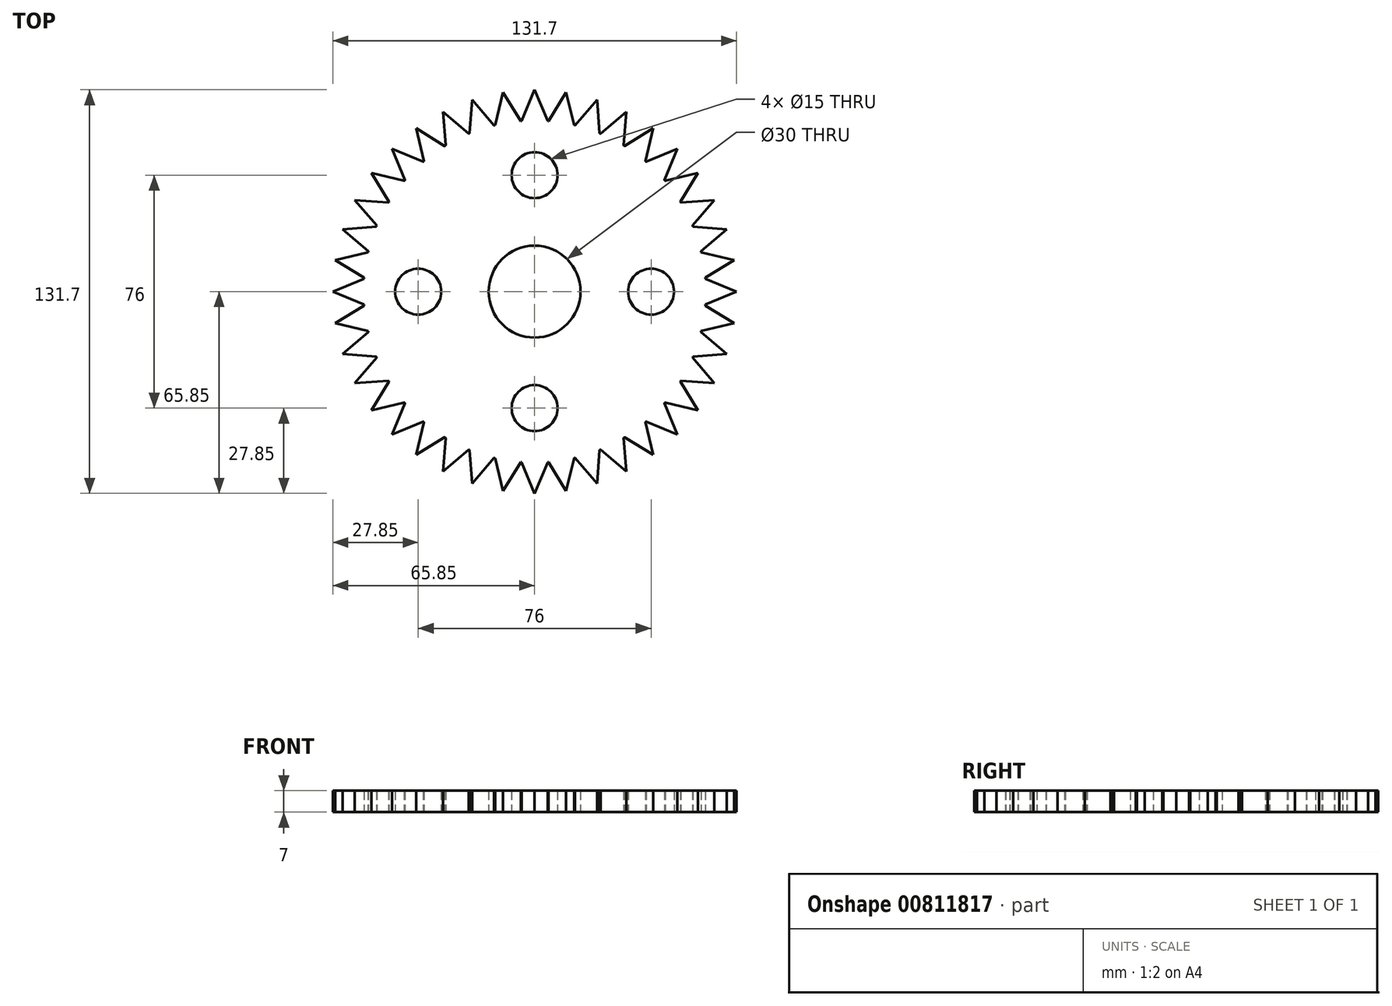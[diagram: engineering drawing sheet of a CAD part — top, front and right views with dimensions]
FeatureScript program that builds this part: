
annotation { "Feature Type Name" : "Feature", "Feature Type Description" : "" }
export const myFeature = defineFeature(function(context is Context, id is Id, definition is map)
    precondition{}
    {
        {
            var Q0;
            Q0=qCreatedBy(makeId("Top.planeOp"),FACE);
            var sketch = newSketch(context, id + "F0", { "sketchPlane" : qUnion([Q0])});
            skCircle(sketch, "E0", {"center": v(0, 0) * mm, "radius": 15 * mm});
            skCircle(sketch, "E1", {"center": v(0, 38) * mm, "radius": 7.5 * mm});
            skCircle(sketch, "E2.1.0", {"center": v(-38, 0) * mm, "radius": 7.5 * mm});
            skCircle(sketch, "E2.2.0", {"center": v(0, -38) * mm, "radius": 7.5 * mm});
            skCircle(sketch, "E2.3.0", {"center": v(38, 0) * mm, "radius": 7.5 * mm});
            skPoint(sketch, "E3.start.orphan", {"position": v(0, 15) * mm});
            skCircle(sketch, "E4", {"center": v(0, 0) * mm, "radius": 55.85 * mm});
            skLineSegment(sketch, "E5", {"start": v(0, 65.85) * mm, "end": v(4.22, 55.7) * mm});
            skLineSegment(sketch, "E6", {"start": v(4.22, 55.7) * mm, "end": v(0, 65.85) * mm});
            skLineSegment(sketch, "E7.MirrorCS", {"start": v(-4.22, 55.7) * mm, "end": v(0, 65.85) * mm});
            skLineSegment(sketch, "E8.1.0", {"start": v(-12.88, 54.35) * mm, "end": v(-10.3, 65.04) * mm});
            skLineSegment(sketch, "E8.1.1", {"start": v(-4.55, 55.67) * mm, "end": v(-10.3, 65.04) * mm});
            skLineSegment(sketch, "E8.2.0", {"start": v(-21.22, 51.67) * mm, "end": v(-20.35, 62.63) * mm});
            skLineSegment(sketch, "E8.2.1", {"start": v(-13.2, 54.27) * mm, "end": v(-20.35, 62.63) * mm});
            skLineSegment(sketch, "E8.3.0", {"start": v(-29.04, 47.7) * mm, "end": v(-29.9, 58.68) * mm});
            skLineSegment(sketch, "E8.3.1", {"start": v(-21.53, 51.54) * mm, "end": v(-29.9, 58.68) * mm});
            skLineSegment(sketch, "E8.4.0", {"start": v(-36.15, 42.58) * mm, "end": v(-38.7, 53.28) * mm});
            skLineSegment(sketch, "E8.4.1", {"start": v(-29.32, 47.54) * mm, "end": v(-38.7, 53.28) * mm});
            skLineSegment(sketch, "E8.5.0", {"start": v(-42.36, 36.4) * mm, "end": v(-46.57, 46.57) * mm});
            skLineSegment(sketch, "E8.5.1", {"start": v(-36.4, 42.36) * mm, "end": v(-46.57, 46.57) * mm});
            skLineSegment(sketch, "E8.6.0", {"start": v(-47.54, 29.32) * mm, "end": v(-53.28, 38.7) * mm});
            skLineSegment(sketch, "E8.6.1", {"start": v(-42.58, 36.15) * mm, "end": v(-53.28, 38.7) * mm});
            skLineSegment(sketch, "E8.7.0", {"start": v(-51.54, 21.53) * mm, "end": v(-58.68, 29.9) * mm});
            skLineSegment(sketch, "E8.7.1", {"start": v(-47.7, 29.04) * mm, "end": v(-58.68, 29.9) * mm});
            skLineSegment(sketch, "E8.8.0", {"start": v(-54.27, 13.2) * mm, "end": v(-62.63, 20.35) * mm});
            skLineSegment(sketch, "E8.8.1", {"start": v(-51.67, 21.22) * mm, "end": v(-62.63, 20.35) * mm});
            skLineSegment(sketch, "E8.9.0", {"start": v(-55.67, 4.55) * mm, "end": v(-65.04, 10.3) * mm});
            skLineSegment(sketch, "E8.9.1", {"start": v(-54.35, 12.88) * mm, "end": v(-65.04, 10.3) * mm});
            skLineSegment(sketch, "E8.10.0", {"start": v(-55.7, -4.22) * mm, "end": v(-65.85, 0) * mm});
            skLineSegment(sketch, "E8.10.1", {"start": v(-55.7, 4.22) * mm, "end": v(-65.85, 0) * mm});
            skLineSegment(sketch, "E8.11.0", {"start": v(-54.35, -12.88) * mm, "end": v(-65.04, -10.3) * mm});
            skLineSegment(sketch, "E8.11.1", {"start": v(-55.67, -4.55) * mm, "end": v(-65.04, -10.3) * mm});
            skLineSegment(sketch, "E8.12.0", {"start": v(-51.67, -21.22) * mm, "end": v(-62.63, -20.35) * mm});
            skLineSegment(sketch, "E8.12.1", {"start": v(-54.27, -13.2) * mm, "end": v(-62.63, -20.35) * mm});
            skLineSegment(sketch, "E8.13.0", {"start": v(-47.7, -29.04) * mm, "end": v(-58.68, -29.9) * mm});
            skLineSegment(sketch, "E8.13.1", {"start": v(-51.54, -21.53) * mm, "end": v(-58.68, -29.9) * mm});
            skLineSegment(sketch, "E8.14.0", {"start": v(-42.58, -36.15) * mm, "end": v(-53.28, -38.7) * mm});
            skLineSegment(sketch, "E8.14.1", {"start": v(-47.54, -29.32) * mm, "end": v(-53.28, -38.7) * mm});
            skLineSegment(sketch, "E9.1.15.0", {"start": v(-36.4, -42.36) * mm, "end": v(-46.57, -46.57) * mm});
            skLineSegment(sketch, "E9.3.15.0", {"start": v(-42.36, -36.4) * mm, "end": v(-46.57, -46.57) * mm});
            skLineSegment(sketch, "E9.1.16.0", {"start": v(-29.32, -47.54) * mm, "end": v(-38.7, -53.28) * mm});
            skLineSegment(sketch, "E9.3.16.0", {"start": v(-36.15, -42.58) * mm, "end": v(-38.7, -53.28) * mm});
            skLineSegment(sketch, "E9.1.17.0", {"start": v(-21.53, -51.54) * mm, "end": v(-29.9, -58.68) * mm});
            skLineSegment(sketch, "E9.3.17.0", {"start": v(-29.04, -47.7) * mm, "end": v(-29.9, -58.68) * mm});
            skLineSegment(sketch, "E9.1.18.0", {"start": v(-13.2, -54.27) * mm, "end": v(-20.35, -62.63) * mm});
            skLineSegment(sketch, "E9.3.18.0", {"start": v(-21.22, -51.67) * mm, "end": v(-20.35, -62.63) * mm});
            skLineSegment(sketch, "E9.1.19.0", {"start": v(-4.55, -55.67) * mm, "end": v(-10.3, -65.04) * mm});
            skLineSegment(sketch, "E9.3.19.0", {"start": v(-12.88, -54.35) * mm, "end": v(-10.3, -65.04) * mm});
            skLineSegment(sketch, "E9.1.20.0", {"start": v(4.22, -55.7) * mm, "end": v(0, -65.85) * mm});
            skLineSegment(sketch, "E9.3.20.0", {"start": v(-4.22, -55.7) * mm, "end": v(0, -65.85) * mm});
            skLineSegment(sketch, "E9.1.21.0", {"start": v(12.88, -54.35) * mm, "end": v(10.3, -65.04) * mm});
            skLineSegment(sketch, "E9.3.21.0", {"start": v(4.55, -55.67) * mm, "end": v(10.3, -65.04) * mm});
            skLineSegment(sketch, "E9.1.22.0", {"start": v(21.22, -51.67) * mm, "end": v(20.35, -62.63) * mm});
            skLineSegment(sketch, "E9.3.22.0", {"start": v(13.2, -54.27) * mm, "end": v(20.35, -62.63) * mm});
            skLineSegment(sketch, "E9.1.23.0", {"start": v(29.04, -47.7) * mm, "end": v(29.9, -58.68) * mm});
            skLineSegment(sketch, "E9.3.23.0", {"start": v(21.53, -51.54) * mm, "end": v(29.9, -58.68) * mm});
            skLineSegment(sketch, "E9.1.24.0", {"start": v(36.15, -42.58) * mm, "end": v(38.7, -53.28) * mm});
            skLineSegment(sketch, "E9.3.24.0", {"start": v(29.32, -47.54) * mm, "end": v(38.7, -53.28) * mm});
            skLineSegment(sketch, "E9.1.25.0", {"start": v(42.36, -36.4) * mm, "end": v(46.57, -46.57) * mm});
            skLineSegment(sketch, "E9.3.25.0", {"start": v(36.4, -42.36) * mm, "end": v(46.57, -46.57) * mm});
            skLineSegment(sketch, "E10.1.26.0", {"start": v(47.54, -29.32) * mm, "end": v(53.28, -38.7) * mm});
            skLineSegment(sketch, "E10.3.26.0", {"start": v(42.58, -36.15) * mm, "end": v(53.28, -38.7) * mm});
            skLineSegment(sketch, "E10.1.27.0", {"start": v(51.54, -21.53) * mm, "end": v(58.68, -29.9) * mm});
            skLineSegment(sketch, "E10.3.27.0", {"start": v(47.7, -29.04) * mm, "end": v(58.68, -29.9) * mm});
            skLineSegment(sketch, "E11.1.28.0", {"start": v(54.27, -13.2) * mm, "end": v(62.63, -20.35) * mm});
            skLineSegment(sketch, "E11.3.28.0", {"start": v(51.67, -21.22) * mm, "end": v(62.63, -20.35) * mm});
            skLineSegment(sketch, "E11.1.29.0", {"start": v(55.67, -4.55) * mm, "end": v(65.04, -10.3) * mm});
            skLineSegment(sketch, "E11.3.29.0", {"start": v(54.35, -12.88) * mm, "end": v(65.04, -10.3) * mm});
            skLineSegment(sketch, "E12.1.30.0", {"start": v(55.7, 4.22) * mm, "end": v(65.85, 0) * mm});
            skLineSegment(sketch, "E12.3.30.0", {"start": v(55.7, -4.22) * mm, "end": v(65.85, 0) * mm});
            skLineSegment(sketch, "E12.1.31.0", {"start": v(54.35, 12.88) * mm, "end": v(65.04, 10.3) * mm});
            skLineSegment(sketch, "E12.3.31.0", {"start": v(55.67, 4.55) * mm, "end": v(65.04, 10.3) * mm});
            skLineSegment(sketch, "E12.1.32.0", {"start": v(51.67, 21.22) * mm, "end": v(62.63, 20.35) * mm});
            skLineSegment(sketch, "E12.3.32.0", {"start": v(54.27, 13.2) * mm, "end": v(62.63, 20.35) * mm});
            skLineSegment(sketch, "E12.1.33.0", {"start": v(47.7, 29.04) * mm, "end": v(58.68, 29.9) * mm});
            skLineSegment(sketch, "E12.3.33.0", {"start": v(51.54, 21.53) * mm, "end": v(58.68, 29.9) * mm});
            skLineSegment(sketch, "E13.1.34.0", {"start": v(42.58, 36.15) * mm, "end": v(53.28, 38.7) * mm});
            skLineSegment(sketch, "E13.3.34.0", {"start": v(47.54, 29.32) * mm, "end": v(53.28, 38.7) * mm});
            skLineSegment(sketch, "E13.1.35.0", {"start": v(36.4, 42.36) * mm, "end": v(46.57, 46.57) * mm});
            skLineSegment(sketch, "E13.3.35.0", {"start": v(42.36, 36.4) * mm, "end": v(46.57, 46.57) * mm});
            skLineSegment(sketch, "E14.1.36.0", {"start": v(29.32, 47.54) * mm, "end": v(38.7, 53.28) * mm});
            skLineSegment(sketch, "E14.3.36.0", {"start": v(36.15, 42.58) * mm, "end": v(38.7, 53.28) * mm});
            skLineSegment(sketch, "E15.1.37.0", {"start": v(21.53, 51.54) * mm, "end": v(29.9, 58.68) * mm});
            skLineSegment(sketch, "E15.3.37.0", {"start": v(29.04, 47.7) * mm, "end": v(29.9, 58.68) * mm});
            skLineSegment(sketch, "E15.1.38.0", {"start": v(13.2, 54.27) * mm, "end": v(20.35, 62.63) * mm});
            skLineSegment(sketch, "E15.3.38.0", {"start": v(21.22, 51.67) * mm, "end": v(20.35, 62.63) * mm});
            skLineSegment(sketch, "E15.1.39.0", {"start": v(4.55, 55.67) * mm, "end": v(10.3, 65.04) * mm});
            skLineSegment(sketch, "E15.3.39.0", {"start": v(12.88, 54.35) * mm, "end": v(10.3, 65.04) * mm});
            skSolve(sketch);
        }
        {
            var Q0;
            Q0 = qSketchRegion(id + "F0", true);
            extrude(context, id + "F1", {"entities" : qUnion([Q0]), "depth" : 7 * mm, "offsetDistance" : 25 * mm});
        }
    });
